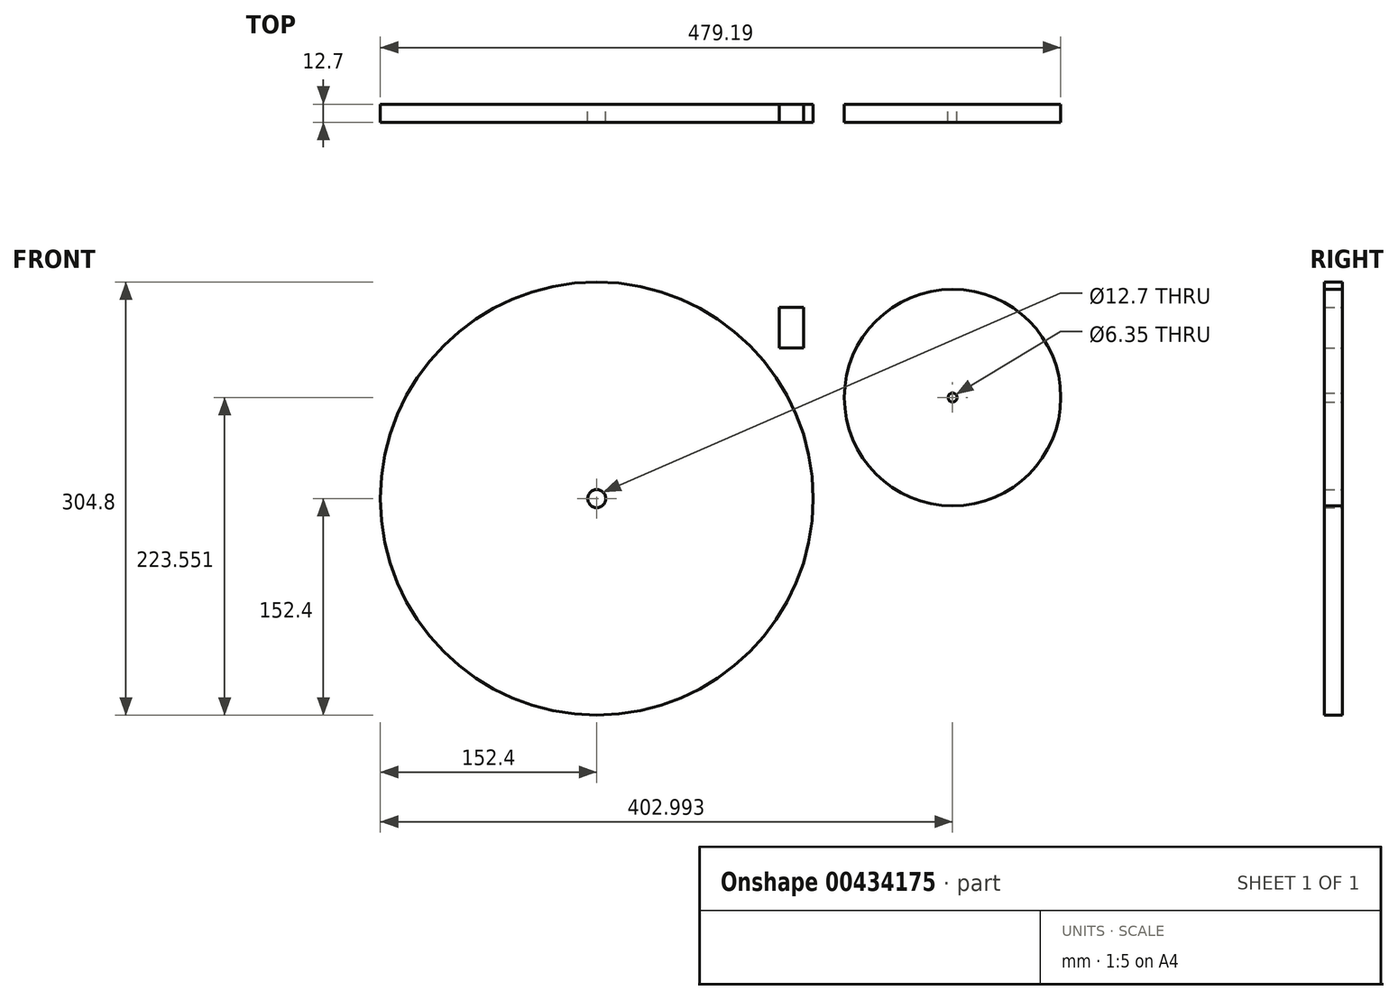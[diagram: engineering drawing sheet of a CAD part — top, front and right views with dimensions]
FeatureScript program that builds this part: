
annotation { "Feature Type Name" : "Feature", "Feature Type Description" : "" }
export const myFeature = defineFeature(function(context is Context, id is Id, definition is map)
    precondition{}
    {
        {
            var Q0;
            Q0=qCreatedBy(makeId("Front.planeOp"),FACE);
            var sketch = newSketch(context, id + "F0", { "sketchPlane" : qUnion([Q0])});
            skCircle(sketch, "E0", {"center": v(0, 0) * mm, "radius": 152.4 * mm});
            skCircle(sketch, "E1", {"center": v(0, 0) * mm, "radius": 6.35 * mm});
            skCircle(sketch, "E2", {"center": v(250.6, 71.15) * mm, "radius": 76.2 * mm});
            skCircle(sketch, "E3", {"center": v(250.6, 71.15) * mm, "radius": 3.18 * mm});
            skLineSegment(sketch, "E4.bottom", {"start": v(128.5, 134.58) * mm, "end": v(145.82, 134.58) * mm});
            skLineSegment(sketch, "E4.top", {"start": v(128.5, 106.19) * mm, "end": v(145.82, 106.19) * mm});
            skLineSegment(sketch, "E4.left", {"start": v(128.5, 134.58) * mm, "end": v(128.5, 106.19) * mm});
            skLineSegment(sketch, "E4.right", {"start": v(145.82, 134.58) * mm, "end": v(145.82, 106.19) * mm});
            skSolve(sketch);
        }
        {
            var Q0;
            Q0 = qSketchRegion(id + "F0", true);
            extrude(context, id + "F1", {"entities" : qUnion([Q0]), "depth" : 12.7 * mm});
        }
    });
